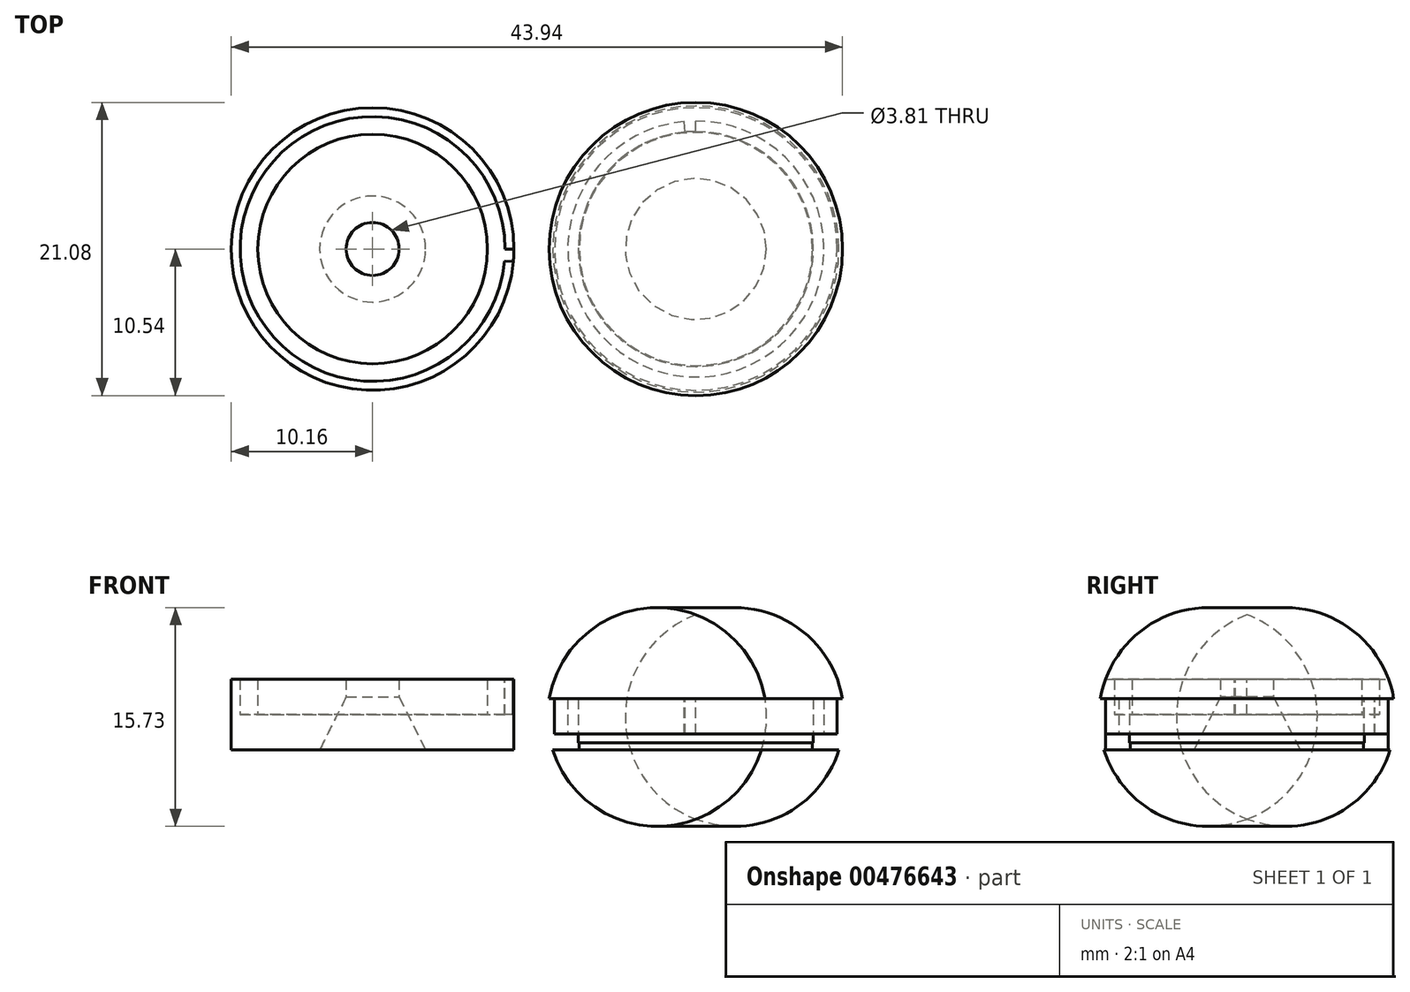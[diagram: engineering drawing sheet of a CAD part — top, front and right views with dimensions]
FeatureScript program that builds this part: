
annotation { "Feature Type Name" : "Feature", "Feature Type Description" : "" }
export const myFeature = defineFeature(function(context is Context, id is Id, definition is map)
    precondition{}
    {
        {
            var Q0;
            Q0=qCreatedBy(makeId("Front.planeOp"),FACE);
            var sketch = newSketch(context, id + "F0", { "sketchPlane" : qUnion([Q0])});
            skLineSegment(sketch, "E0", {"start": v(0, 0) * mm, "end": v(0, 5.08) * mm});
            skLineSegment(sketch, "E1", {"start": v(0, 5.08) * mm, "end": v(-0.63, 5.08) * mm});
            skLineSegment(sketch, "E2", {"start": v(-0.64, 5.08) * mm, "end": v(-0.63, 2.54) * mm});
            skLineSegment(sketch, "E3", {"start": v(-0.63, 2.54) * mm, "end": v(-1.9, 2.54) * mm});
            skLineSegment(sketch, "E4", {"start": v(-1.9, 2.54) * mm, "end": v(-1.9, 5.08) * mm});
            skLineSegment(sketch, "E5", {"start": v(-1.9, 5.08) * mm, "end": v(-8.26, 5.08) * mm});
            skLineSegment(sketch, "E6", {"start": v(-8.26, 5.08) * mm, "end": v(-8.26, 3.81) * mm});
            skLineSegment(sketch, "E7", {"start": v(-8.26, 3.81) * mm, "end": v(-6.35, 0) * mm});
            skLineSegment(sketch, "E8", {"start": v(-6.35, 0) * mm, "end": v(0, 0) * mm});
            skLineSegment(sketch, "E9", {"start": v(-10.16, 0) * mm, "end": v(-10.16, 5.2) * mm});
            skSolve(sketch);
        }
        {
            var Q0;
            Q0=makeQuery(id+"F0.imprint","IMPRINT",FACE,{"disambiguationData":[TD([[makeQuery(id+"F0.imprint","IMPRINT",EDGE,{"derivedFrom":sQuery(id+"F0.wireOp",EDGE,"E0")}),1.0]])]});
            var Q1;
            Q1=sQuery(id+"F0.wireOp",EDGE,"E9");
            revolve(context, id + "F1", {"entities" : qUnion([Q0]), "axis" : qUnion([Q1]), "revolveType" : RevolveType.FULL});
        }
        {
            var Q0;
            Q0=makeQuery(id+"F1.opRevolve","SWEPT_FACE",FACE,{"disambiguationData":[OSD([sQuery(id+"F0.wireOp",EDGE,"E1")])]});
            var sketch = newSketch(context, id + "F2", { "sketchPlane" : qUnion([Q0])});
            skArc(sketch, "E10", {"start": v(-0.78, -0.84) * mm, "mid": v(-0.76, -0.42) * mm, "end": v(-0.75, 0) * mm});
            skArc(sketch, "E11", {"start": v(0.23, -0.94) * mm, "mid": v(0.26, -0.47) * mm, "end": v(0.27, 0) * mm});
            skLineSegment(sketch, "E12", {"start": v(-0.75, 0) * mm, "end": v(0.27, 0) * mm});
            skLineSegment(sketch, "E13", {"start": v(-0.78, -0.84) * mm, "end": v(0.23, -0.94) * mm});
            skSolve(sketch);
        }
        {
            var Q0;
            {var subQ0=sQuery(id+"F2.wireOp",EDGE,"E12");var subQ1=sQuery(id+"F0.wireOp",EDGE,"E1");var subQ2=makeQuery(id+"F1.opRevolve","SWEPT_EDGE",EDGE,{"disambiguationData":[OSD([sQuery(id+"F0.wireOp",EDGE,"E0"),subQ1])]});var subQ3=makeQuery(id+"F2.imprint","INTERSECT",VERTEX,{"derivedFrom":[subQ2,subQ0]});Q0=makeQuery(id+"F2.imprint","IMPRINT",FACE,{"disambiguationData":[TD([[makeQuery(id+"F2.imprint","IMPRINT",EDGE,{"disambiguationData":[TD([[subQ3,1.0]])],"derivedFrom":subQ0}),-1.0]])]});}
            var Q1;
            Q1=makeQuery(id+"F1.opRevolve","SWEPT_FACE",FACE,{"disambiguationData":[OSD([sQuery(id+"F0.wireOp",EDGE,"E3")])]});
            extrude(context, id + "F3", {"entities" : qUnion([Q0]), "operationType" : NewBodyOperationType.REMOVE, "endBound" : BoundingType.UP_TO_SURFACE, "oppositeDirection" : true, "endBoundEntityFace" : qUnion([Q1]), "depth" : 25.4 * mm});
        }
        {
            var Q0;
            Q0=qCreatedBy(makeId("Front.planeOp"),FACE);
            var sketch = newSketch(context, id + "F4", { "sketchPlane" : qUnion([Q0])});
            skLineSegment(sketch, "E14", {"start": v(4.7, 0) * mm, "end": v(4.7, 0.5) * mm});
            skLineSegment(sketch, "E15", {"start": v(4.7, 0.5) * mm, "end": v(4.64, 0.5) * mm});
            skLineSegment(sketch, "E16", {"start": v(4.64, 0.5) * mm, "end": v(4.64, 3.68) * mm});
            skLineSegment(sketch, "E17", {"start": v(4.64, 3.68) * mm, "end": v(3.87, 3.68) * mm});
            skLineSegment(sketch, "E18", {"start": v(3.87, 3.68) * mm, "end": v(3.87, 1.14) * mm});
            skLineSegment(sketch, "E19", {"start": v(3.87, 1.14) * mm, "end": v(2.92, 1.14) * mm});
            skLineSegment(sketch, "E20", {"start": v(2.92, 1.14) * mm, "end": v(2.92, 3.68) * mm});
            skLineSegment(sketch, "E21", {"start": v(2.92, 3.68) * mm, "end": v(2.54, 3.68) * mm});
            skLineSegment(sketch, "E22", {"start": v(4.7, 0) * mm, "end": v(2.8, 0) * mm});
            skArc(sketch, "E23", {"start": v(2.54, 3.68) * mm, "mid": v(2.45, 1.83) * mm, "end": v(2.8, 0) * mm});
            skLineSegment(sketch, "E24", {"start": v(13.08, 0) * mm, "end": v(13.08, 2.75) * mm});
            skSolve(sketch);
        }
        {
            var Q0;
            Q0=makeQuery(id+"F4.imprint","IMPRINT",FACE,{"disambiguationData":[TD([[makeQuery(id+"F4.imprint","IMPRINT",EDGE,{"derivedFrom":sQuery(id+"F4.wireOp",EDGE,"E14")}),1.0]])]});
            var Q1;
            Q1=sQuery(id+"F4.wireOp",EDGE,"E24");
            revolve(context, id + "F5", {"entities" : qUnion([Q0]), "axis" : qUnion([Q1]), "revolveType" : RevolveType.FULL});
        }
        {
            var Q0;
            Q0=makeQuery(id+"F5.opRevolve","SWEPT_FACE",FACE,{"disambiguationData":[OSD([sQuery(id+"F4.wireOp",EDGE,"E17")])]});
            var sketch = newSketch(context, id + "F6", { "sketchPlane" : qUnion([Q0])});
            skArc(sketch, "E25", {"start": v(13.08, 5.99) * mm, "mid": v(12.81, 5.98) * mm, "end": v(12.54, 5.96) * mm});
            skArc(sketch, "E26", {"start": v(13.08, 9.2) * mm, "mid": v(12.67, 9.2) * mm, "end": v(12.26, 9.17) * mm});
            skLineSegment(sketch, "E27", {"start": v(13.08, 5.99) * mm, "end": v(13.08, 9.2) * mm});
            skLineSegment(sketch, "E28", {"start": v(12.54, 5.96) * mm, "end": v(12.26, 9.17) * mm});
            skSolve(sketch);
        }
        {
            var Q0;
            {var subQ0=sQuery(id+"F6.wireOp",EDGE,"E26");Q0=makeQuery(id+"F6.imprint","IMPRINT",FACE,{"disambiguationData":[TD([[makeQuery(id+"F6.imprint","IMPRINT",EDGE,{"derivedFrom":subQ0}),-1.0]])]});}
            var Q1;
            Q1=makeQuery(id+"F5.opRevolve","SWEPT_FACE",FACE,{"disambiguationData":[OSD([sQuery(id+"F4.wireOp",EDGE,"E19")])]});
            extrude(context, id + "F7", {"entities" : qUnion([Q0]), "operationType" : NewBodyOperationType.REMOVE, "endBound" : BoundingType.UP_TO_SURFACE, "oppositeDirection" : true, "endBoundEntityFace" : qUnion([Q1]), "depth" : 25.4 * mm});
        }
    });
